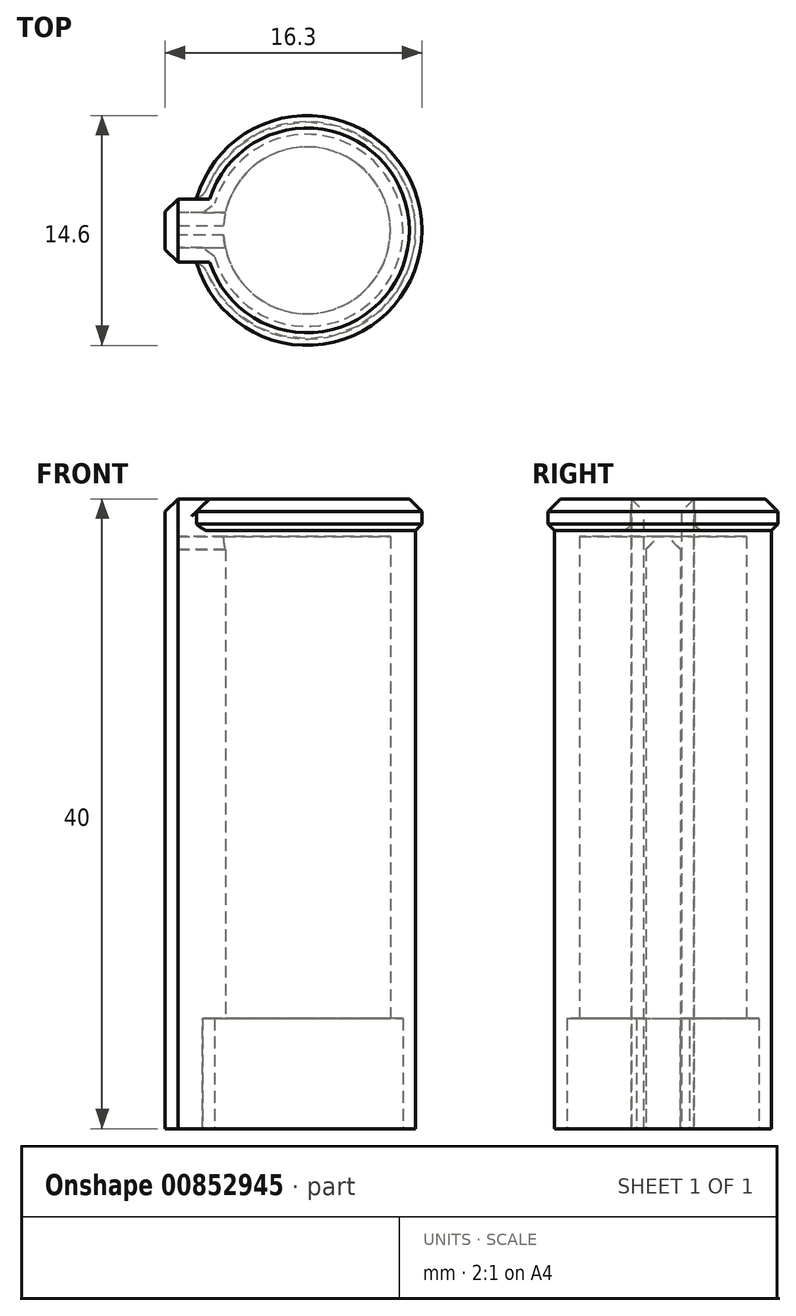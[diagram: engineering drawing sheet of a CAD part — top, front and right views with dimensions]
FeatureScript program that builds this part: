
annotation { "Feature Type Name" : "Feature", "Feature Type Description" : "" }
export const myFeature = defineFeature(function(context is Context, id is Id, definition is map)
    precondition{}
    {
        {
            var Q0;
            Q0=qCreatedBy(makeId("Top.planeOp"),FACE);
            var sketch = newSketch(context, id + "F0", { "sketchPlane" : qUnion([Q0])});
            skCircle(sketch, "E0", {"center": v(0, 0) * mm, "radius": 6.9 * mm});
            skSolve(sketch);
        }
        {
            var Q0;
            Q0=makeQuery(id+"F0.imprint","IMPRINT",FACE,{"disambiguationData":[TD([[makeQuery(id+"F0.imprint","IMPRINT",EDGE,{"derivedFrom":sQuery(id+"F0.wireOp",EDGE,"E0")}),1.0]])]});
            extrude(context, id + "F1", {"entities" : qUnion([Q0]), "depth" : 40 * mm, "offsetDistance" : 25 * mm});
        }
        {
            var Q0;
            Q0=qCreatedBy(makeId("Top.planeOp"),FACE);
            var sketch = newSketch(context, id + "F2", { "sketchPlane" : qUnion([Q0])});
            skLineSegment(sketch, "E1.bottom", {"start": v(-9, 1.98) * mm, "end": v(0, 1.98) * mm});
            skLineSegment(sketch, "E1.top", {"start": v(-9, -2.02) * mm, "end": v(0, -2.02) * mm});
            skLineSegment(sketch, "E1.left", {"start": v(-9, 1.98) * mm, "end": v(-9, -2.02) * mm});
            skLineSegment(sketch, "E1.right", {"start": v(0, 1.98) * mm, "end": v(0, -2.02) * mm});
            skSolve(sketch);
        }
        {
            var Q0;
            Q0 = qSketchRegion(id + "F2", true);
            extrude(context, id + "F3", {"entities" : qUnion([Q0]), "operationType" : NewBodyOperationType.ADD, "depth" : 40 * mm, "offsetDistance" : 25 * mm});
        }
        {
            var Q0;
            Q0=qCreatedBy(makeId("Top.planeOp"),FACE);
            var sketch = newSketch(context, id + "F4", { "sketchPlane" : qUnion([Q0])});
            skCircle(sketch, "E2", {"center": v(0, 0) * mm, "radius": 6.1 * mm});
            skSolve(sketch);
        }
        {
            var Q0;
            Q0 = qSketchRegion(id + "F4", true);
            var Q1;
            Q1=sQuery(id+"F4.wireOp",EDGE,"E2");
            extrude(context, id + "F5", {"entities" : qUnion([Q0]), "operationType" : NewBodyOperationType.REMOVE, "surfaceEntities" : qUnion([Q1]), "depth" : 7 * mm, "offsetDistance" : 25 * mm});
        }
        {
            var Q0;
            Q0=qCreatedBy(makeId("Top.planeOp"),FACE);
            var sketch = newSketch(context, id + "F6", { "sketchPlane" : qUnion([Q0])});
            skLineSegment(sketch, "E3.bottom", {"start": v(4.8, 1.11) * mm, "end": v(-8.2, 1.11) * mm});
            skLineSegment(sketch, "E3.top", {"start": v(4.8, -1.09) * mm, "end": v(-8.2, -1.09) * mm});
            skLineSegment(sketch, "E3.left", {"start": v(4.8, 1.11) * mm, "end": v(4.8, -1.09) * mm});
            skLineSegment(sketch, "E3.right", {"start": v(-8.2, 1.11) * mm, "end": v(-8.2, -1.09) * mm});
            skSolve(sketch);
        }
        {
            var Q0;
            Q0 = qSketchRegion(id + "F6", true);
            extrude(context, id + "F7", {"entities" : qUnion([Q0]), "operationType" : NewBodyOperationType.REMOVE, "depth" : 37.6 * mm, "offsetDistance" : 25 * mm});
        }
        {
            var Q0;
            Q0=qCreatedBy(makeId("Top.planeOp"),FACE);
            var sketch = newSketch(context, id + "F8", { "sketchPlane" : qUnion([Q0])});
            skCircle(sketch, "E4", {"center": v(0, 0) * mm, "radius": 5.3 * mm});
            skSolve(sketch);
        }
        {
            var Q0;
            Q0 = qSketchRegion(id + "F8", true);
            extrude(context, id + "F9", {"entities" : qUnion([Q0]), "operationType" : NewBodyOperationType.REMOVE, "depth" : 37.6 * mm, "offsetDistance" : 25 * mm});
        }
        {
            var Q0;
            Q0=qCreatedBy(makeId("Top.planeOp"),FACE);
            cPlane(context, id + "F10", {"entities" : qUnion([Q0]), "cplaneType" : CPlaneType.OFFSET, "offset" : 40 * mm, "width" : 150 * mm, "height" : 150 * mm});
        }
        {
            var Q0;
            Q0=qCreatedBy(id+"F10.planeOp",FACE);
            var sketch = newSketch(context, id + "F11", { "sketchPlane" : qUnion([Q0])});
            skCircle(sketch, "E5", {"center": v(0, 0) * mm, "radius": 7.3 * mm});
            skSolve(sketch);
        }
        {
            var Q0;
            Q0 = qSketchRegion(id + "F11", true);
            extrude(context, id + "F12", {"entities" : qUnion([Q0]), "operationType" : NewBodyOperationType.ADD, "oppositeDirection" : true, "depth" : 2.4 * mm, "offsetDistance" : 25 * mm});
        }
        {
            var Q0;
            Q0=makeQuery(id+"F12.opExtrude","CAP_EDGE",EDGE,{"disambiguationData":[OSD([sQuery(id+"F11.wireOp",EDGE,"E5")])],"isStart":true});
            var Q1;
            Q1=makeQuery(id+"F12.opExtrude","CAP_EDGE",EDGE,{"disambiguationData":[OSD([sQuery(id+"F11.wireOp",EDGE,"E5")])],"isStart":false});
            chamfer(context, id + "F13", {"entities" : qUnion([Q0, Q1]), "width" : .8 * mm, "tangentPropagation" : true});
        }
        {
            var Q0;
            Q0=makeQuery(id+"F3.opExtrude","SWEPT_EDGE",EDGE,{"disambiguationData":[OSD([sQuery(id+"F2.wireOp",EDGE,"E1.bottom"),sQuery(id+"F2.wireOp",EDGE,"E1.left")])]});
            var Q1;
            Q1=makeQuery(id+"F3.opExtrude","SWEPT_EDGE",EDGE,{"disambiguationData":[OSD([sQuery(id+"F2.wireOp",EDGE,"E1.top"),sQuery(id+"F2.wireOp",EDGE,"E1.left")])]});
            var Q2;
            Q2=makeQuery(id+"F3.opExtrude","CAP_EDGE",EDGE,{"disambiguationData":[OSD([sQuery(id+"F2.wireOp",EDGE,"E1.left")])],"isStart":false});
            chamfer(context, id + "F14", {"entities" : qUnion([Q0, Q1, Q2]), "width" : .8 * mm, "tangentPropagation" : true});
        }
        {
            var Q0;
            Q0=makeQuery(id+"F7.boolean.opBoolean","INTERSECT",EDGE,{"derivedFrom":[makeQuery(id+"F5.boolean.opBoolean","COPY",FACE,{"derivedFrom":makeQuery(id+"F5.opExtrude","SWEPT_FACE",FACE,{"disambiguationData":[OSD([sQuery(id+"F4.wireOp",EDGE,"E2")])]})}),makeQuery(id+"F7.opExtrude","SWEPT_FACE",FACE,{"disambiguationData":[OSD([sQuery(id+"F6.wireOp",EDGE,"E3.top")])]})]});
            var Q1;
            Q1=makeQuery(id+"F7.boolean.opBoolean","INTERSECT",EDGE,{"derivedFrom":[makeQuery(id+"F5.boolean.opBoolean","COPY",FACE,{"derivedFrom":makeQuery(id+"F5.opExtrude","SWEPT_FACE",FACE,{"disambiguationData":[OSD([sQuery(id+"F4.wireOp",EDGE,"E2")])]})}),makeQuery(id+"F7.opExtrude","SWEPT_FACE",FACE,{"disambiguationData":[OSD([sQuery(id+"F6.wireOp",EDGE,"E3.bottom")])]})]});
            chamfer(context, id + "F15", {"entities" : qUnion([Q0, Q1]), "width" : .8 * mm, "tangentPropagation" : true});
        }
        {
            var Q0;
            {var subQ1=sQuery(id+"F6.wireOp",EDGE,"E3.right");var subQ2=sQuery(id+"F6.wireOp",EDGE,"E3.top");Q0=makeQuery(id+"F9.boolean.opBoolean","SPLIT",EDGE,{"disambiguationData":[TD([makeQuery(id+"F7.boolean.opBoolean","COPY",FACE,{"derivedFrom":makeQuery(id+"F7.opExtrude","SWEPT_FACE",FACE,{"disambiguationData":[OSD([subQ1])]})})])],"derivedFrom":makeQuery(id+"F7.boolean.opBoolean","COPY",EDGE,{"derivedFrom":makeQuery(id+"F7.opExtrude","CAP_EDGE",EDGE,{"disambiguationData":[OSD([subQ2])],"isStart":false})})});}
            var Q1;
            {var subQ1=sQuery(id+"F6.wireOp",EDGE,"E3.right");var subQ2=sQuery(id+"F6.wireOp",EDGE,"E3.bottom");Q1=makeQuery(id+"F9.boolean.opBoolean","SPLIT",EDGE,{"disambiguationData":[TD([makeQuery(id+"F7.boolean.opBoolean","COPY",FACE,{"derivedFrom":makeQuery(id+"F7.opExtrude","SWEPT_FACE",FACE,{"disambiguationData":[OSD([subQ1])]})})])],"derivedFrom":makeQuery(id+"F7.boolean.opBoolean","COPY",EDGE,{"derivedFrom":makeQuery(id+"F7.opExtrude","CAP_EDGE",EDGE,{"disambiguationData":[OSD([subQ2])],"isStart":false})})});}
            chamfer(context, id + "F16", {"entities" : qUnion([Q0, Q1]), "width" : .8 * mm, "tangentPropagation" : true});
        }
        {
            var Q0;
            Q0=makeQuery(id+"F3.boolean.opBoolean","INTERSECT",EDGE,{"derivedFrom":[makeQuery(id+"F1.opExtrude","SWEPT_FACE",FACE,{"disambiguationData":[OSD([sQuery(id+"F0.wireOp",EDGE,"E0")])]}),makeQuery(id+"F3.opExtrude","SWEPT_FACE",FACE,{"disambiguationData":[OSD([sQuery(id+"F2.wireOp",EDGE,"E1.top")])]})]});
            fillet(context, id + "F17", {"entities" : qUnion([Q0]), "radius" : 1 * mm, "tangentPropagation" : true, "allowEdgeOverflow" : false});
        }
        {
            var Q0;
            Q0=makeQuery(id+"F3.boolean.opBoolean","INTERSECT",EDGE,{"derivedFrom":[makeQuery(id+"F1.opExtrude","SWEPT_FACE",FACE,{"disambiguationData":[OSD([sQuery(id+"F0.wireOp",EDGE,"E0")])]}),makeQuery(id+"F3.opExtrude","SWEPT_FACE",FACE,{"disambiguationData":[OSD([sQuery(id+"F2.wireOp",EDGE,"E1.bottom")])]})]});
            fillet(context, id + "F18", {"entities" : qUnion([Q0]), "radius" : 1 * mm, "tangentPropagation" : true, "allowEdgeOverflow" : false});
        }
    });
